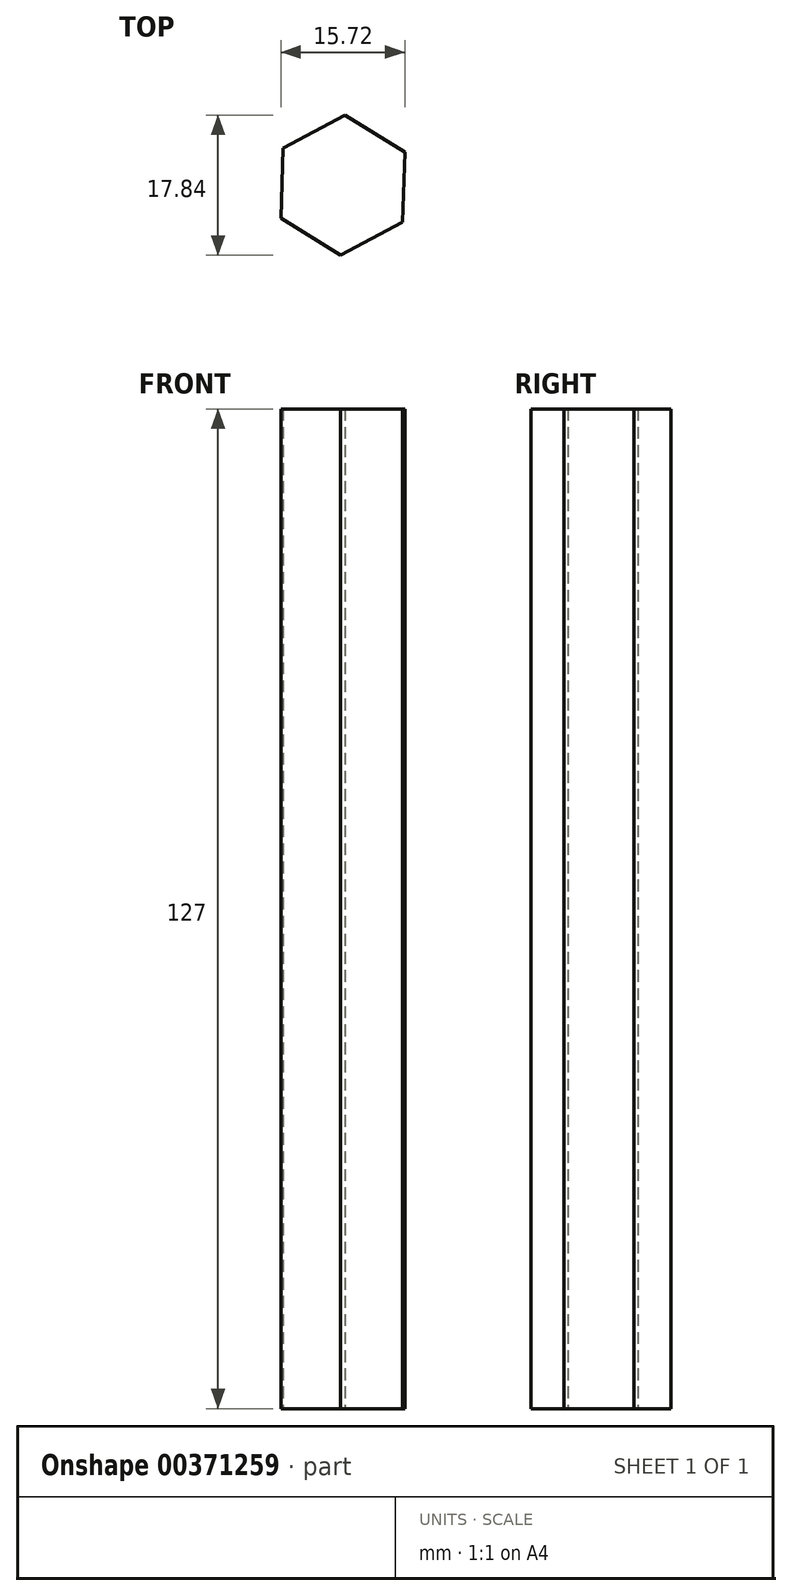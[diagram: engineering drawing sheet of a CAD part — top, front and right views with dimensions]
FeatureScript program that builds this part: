
annotation { "Feature Type Name" : "Feature", "Feature Type Description" : "" }
export const myFeature = defineFeature(function(context is Context, id is Id, definition is map)
    precondition{}
    {
        {
            var Q0;
            Q0=qCreatedBy(makeId("Top.planeOp"),FACE);
            var sketch = newSketch(context, id + "F0", { "sketchPlane" : qUnion([Q0])});
            skCircle(sketch, "E0.cCircle", {"center": v(0, 0) * mm, "radius": 7.72 * mm, "construction": true});
            skLineSegment(sketch, "E0.0", {"start": v(-7.58, 4.7) * mm, "end": v(0.28, 8.92) * mm});
            skLineSegment(sketch, "E0.1", {"start": v(0.28, 8.92) * mm, "end": v(7.86, 4.21) * mm});
            skLineSegment(sketch, "E0.2", {"start": v(7.86, 4.21) * mm, "end": v(7.58, -4.7) * mm});
            skLineSegment(sketch, "E0.3", {"start": v(7.58, -4.7) * mm, "end": v(-0.28, -8.92) * mm});
            skLineSegment(sketch, "E0.4", {"start": v(-0.28, -8.92) * mm, "end": v(-7.86, -4.21) * mm});
            skLineSegment(sketch, "E0.5", {"start": v(-7.86, -4.21) * mm, "end": v(-7.58, 4.7) * mm});
            skPoint(sketch, "E0.0.midPoint", {"position": v(-3.65, 6.8) * mm});
            skSolve(sketch);
        }
        {
            var Q0;
            Q0=makeQuery(id+"F0.imprint","IMPRINT",FACE,{"disambiguationData":[TD([[makeQuery(id+"F0.imprint","IMPRINT",EDGE,{"derivedFrom":sQuery(id+"F0.wireOp",EDGE,"E0.0")}),-1.0]])]});
            extrude(context, id + "F1", {"entities" : qUnion([Q0]), "depth" : 127 * mm});
        }
    });
